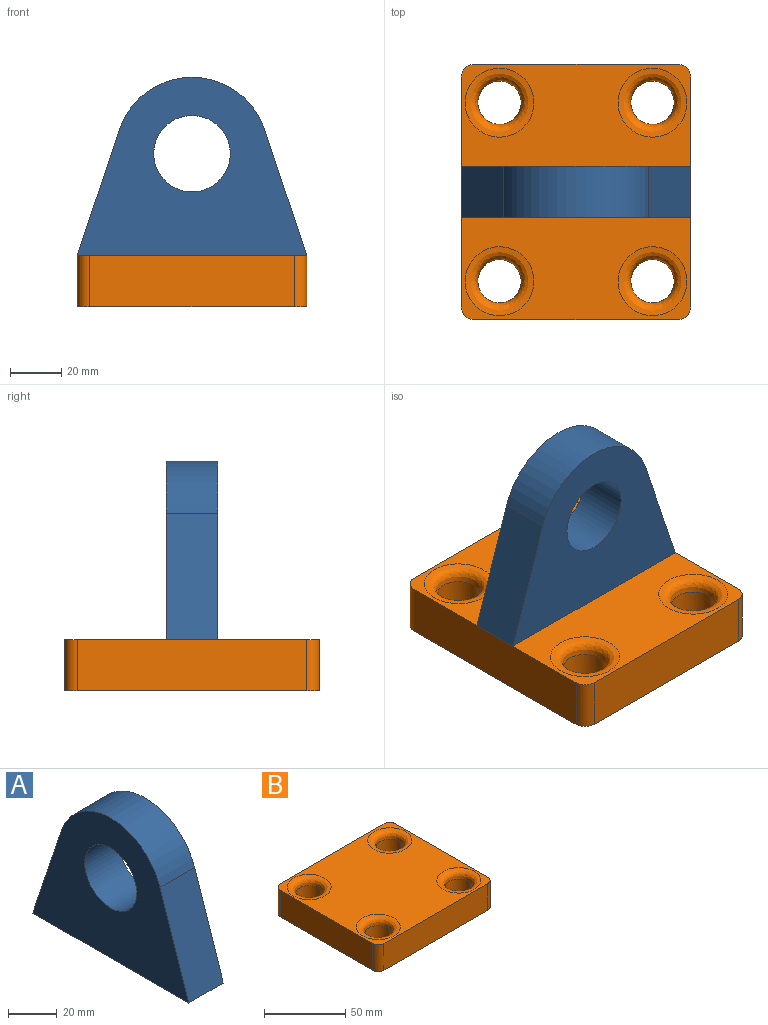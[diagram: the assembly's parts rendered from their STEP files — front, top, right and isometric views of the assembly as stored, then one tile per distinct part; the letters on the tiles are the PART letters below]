
ASSEMBLY  parts=2 mates=1
PART A: 7 faces, bbox 20x90x70 mm
  f0: plane 49.51x20mm, normal (0,-0.95,0.32), area 1044mm2, adj f1,f3,f5,f6
  f1: plane 90x20mm, normal (0,0,-1), area 1800mm2, adj f0,f2,f5,f6
  f2: plane 49.51x20mm, normal (0,0.95,0.32), area 1044mm2, adj f1,f3,f5,f6
  f3: cylinder r=30mm len=56.91mm, axis (-1,0,0), area 1497.9mm2, adj f0,f2,f5,f6
  f4: cylinder r=15mm len=30mm, axis (-1,0,0), area 1885mm2, adj f5,f6
  f5: plane 90x70mm, normal (1,0,0), area 3782.6mm2, adj f0,f1,f2,f3,f4
  f6: plane 90x70mm, normal (-1,0,0), area 3782.6mm2, adj f0,f1,f2,f3,f4
PART B: 18 faces, bbox 100x90x20 mm
  f0: plane 90x20mm, normal (0,1,0), area 1800mm2, adj f1,f11,f12,f13
  f1: cylinder r=5mm len=20mm, axis (0,0,-1), area 157.1mm2, adj f0,f2,f12,f13
  f2: plane 80x20mm, normal (-1,0,0), area 1600mm2, adj f1,f3,f12,f13
  f3: cylinder r=5mm len=20mm, axis (0,0,-1), area 157.1mm2, adj f2,f4,f12,f13
  f4: plane 90x20mm, normal (0,-1,0), area 1800mm2, adj f3,f5,f12,f13
  f5: cylinder r=5mm len=20mm, axis (0,0,-1), area 157.1mm2, adj f4,f6,f12,f13
  f6: plane 80x20mm, normal (1,0,0), area 1600mm2, adj f5,f11,f12,f13
  f7: cylinder r=8.5mm len=17mm, axis (0,0,-1), area 801.1mm2, adj f13,f17
  f8: cylinder r=8.5mm len=17mm, axis (0,0,-1), area 801.1mm2, adj f13,f15
  f9: cylinder r=8.5mm len=17mm, axis (0,0,-1), area 801.1mm2, adj f13,f14
  f10: cylinder r=8.5mm len=17mm, axis (0,0,-1), area 801.1mm2, adj f13,f16
  f11: cylinder r=5mm len=20mm, axis (0,0,-1), area 157.1mm2, adj f0,f6,f12,f13
  f12: plane 100.01x90.01mm, normal (0,0,1), area 6689.4mm2, adj f0,f1,f2,f3,f4,f5,f6,f11
  f13: plane 100x90mm, normal (0,0,-1), area 8070.6mm2, adj f0,f1,f2,f3,f4,f5,f6,f7
  f14: bspline ~27x27mm, area 520.5mm2, adj f9,f12
  f15: bspline ~27x27mm, area 520.5mm2, adj f8,f12
  f16: bspline ~27x27mm, area 520.5mm2, adj f10,f12
  f17: bspline ~27x27mm, area 520.5mm2, adj f7,f12
PLACE A rot(axis=(0,0,-1),90deg) t=(-6.74,-52.94,-52.6)mm
PLACE B rot(axis=(0,0,-1),90deg) t=(-6.74,-62.94,-72.6)mm
MATE planar B.f12 <-> A.f1  axis (0,0,1) through (-6.74,-62.94,-52.6)mm
